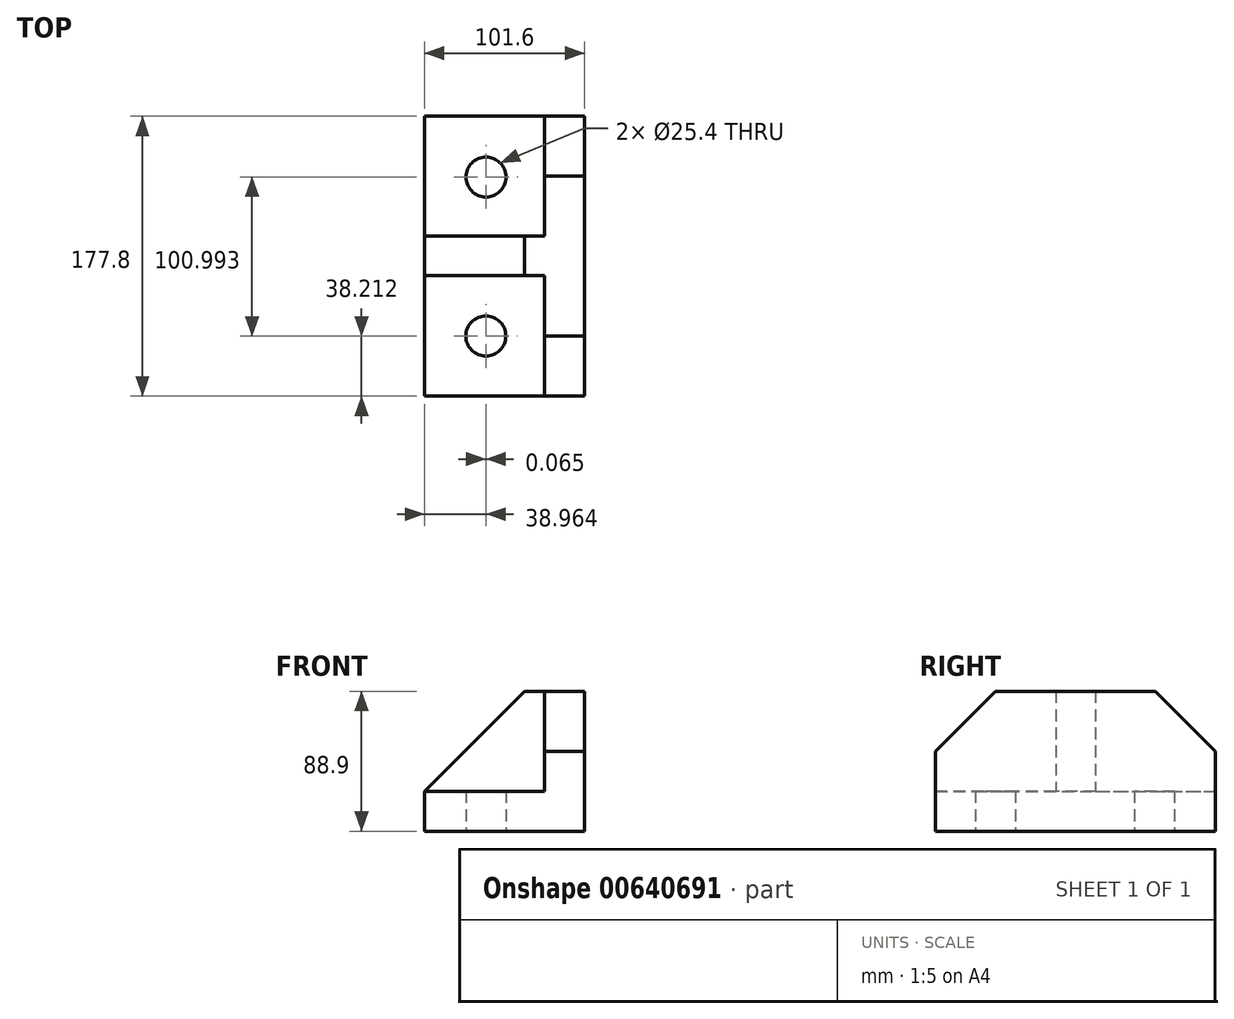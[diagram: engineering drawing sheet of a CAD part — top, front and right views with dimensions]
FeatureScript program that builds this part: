
annotation { "Feature Type Name" : "Feature", "Feature Type Description" : "" }
export const myFeature = defineFeature(function(context is Context, id is Id, definition is map)
    precondition{}
    {
        {
            var Q0;
            Q0=qCreatedBy(makeId("Top.planeOp"),FACE);
            var sketch = newSketch(context, id + "F0", { "sketchPlane" : qUnion([Q0])});
            skLineSegment(sketch, "E0", {"start": v(-50.08, -90.37) * mm, "end": v(51.52, -90.37) * mm});
            skLineSegment(sketch, "E1", {"start": v(-50.08, -90.37) * mm, "end": v(-50.08, 87.43) * mm});
            skLineSegment(sketch, "E2", {"start": v(-50.08, 87.43) * mm, "end": v(51.52, 87.43) * mm});
            skLineSegment(sketch, "E3", {"start": v(51.52, 87.43) * mm, "end": v(51.52, -90.37) * mm});
            skLineSegment(sketch, "E4", {"start": v(-50.08, 11.23) * mm, "end": v(51.52, 11.23) * mm});
            skLineSegment(sketch, "E5", {"start": v(51.52, -14.17) * mm, "end": v(-50.08, -14.17) * mm});
            skLineSegment(sketch, "E6", {"start": v(26.12, 87.43) * mm, "end": v(26.12, -90.37) * mm});
            skLineSegment(sketch, "E7", {"start": v(26.12, 49.33) * mm, "end": v(26.12, -52.27) * mm});
            skLineSegment(sketch, "E8", {"start": v(26.12, 49.33) * mm, "end": v(51.52, 49.33) * mm});
            skLineSegment(sketch, "E9", {"start": v(26.12, -52.27) * mm, "end": v(51.52, -52.27) * mm});
            skCircle(sketch, "E10", {"center": v(-11.05, 48.83) * mm, "radius": 12.7 * mm});
            skCircle(sketch, "E11", {"center": v(-11.12, -52.16) * mm, "radius": 12.7 * mm});
            skSolve(sketch);
        }
        {
            var Q0;
            {var subQ0=sQuery(id+"F0.wireOp",EDGE,"E4");var subQ1=sQuery(id+"F0.wireOp",EDGE,"E3");var subQ2=makeQuery(id+"F0.imprint","INTERSECT",VERTEX,{"derivedFrom":[subQ1,subQ0]});Q0=makeQuery(id+"F0.imprint","IMPRINT",FACE,{"disambiguationData":[TD([[makeQuery(id+"F0.imprint","IMPRINT",EDGE,{"disambiguationData":[TD([[subQ2,-1.0]])],"derivedFrom":subQ1}),-1.0]])]});}
            var Q1;
            {var subQ3=sQuery(id+"F0.wireOp",EDGE,"E8");Q1=makeQuery(id+"F0.imprint","IMPRINT",FACE,{"disambiguationData":[TD([[makeQuery(id+"F0.imprint","IMPRINT",EDGE,{"derivedFrom":subQ3}),-1.0]])]});}
            var Q2;
            {var subQ3=sQuery(id+"F0.wireOp",EDGE,"E9");Q2=makeQuery(id+"F0.imprint","IMPRINT",FACE,{"disambiguationData":[TD([[makeQuery(id+"F0.imprint","IMPRINT",EDGE,{"derivedFrom":subQ3}),1.0]])]});}
            extrude(context, id + "F1", {"entities" : qUnion([Q0, Q1, Q2]), "depth" : 88.9 * mm, "offsetDistance" : 25.4 * mm});
        }
        {
            var Q0;
            {var subQ1=sQuery(id+"F0.wireOp",EDGE,"E2");var subQ5=sQuery(id+"F0.wireOp",EDGE,"E1");var subQ6=makeQuery(id+"F0.imprint","INTERSECT",VERTEX,{"derivedFrom":[subQ5,subQ1]});Q0=makeQuery(id+"F0.imprint","IMPRINT",FACE,{"disambiguationData":[TD([[makeQuery(id+"F0.imprint","IMPRINT",EDGE,{"disambiguationData":[TD([[subQ6,1.0]])],"derivedFrom":subQ5}),-1.0]])]});}
            var Q1;
            {var subQ0=sQuery(id+"F0.wireOp",EDGE,"E4");var subQ1=sQuery(id+"F0.wireOp",EDGE,"E1");var subQ2=makeQuery(id+"F0.imprint","INTERSECT",VERTEX,{"derivedFrom":[subQ1,subQ0]});Q1=makeQuery(id+"F0.imprint","IMPRINT",FACE,{"disambiguationData":[TD([[makeQuery(id+"F0.imprint","IMPRINT",EDGE,{"disambiguationData":[TD([[subQ2,1.0]])],"derivedFrom":subQ1}),-1.0]])]});}
            var Q2;
            {var subQ1=sQuery(id+"F0.wireOp",EDGE,"E0");var subQ5=sQuery(id+"F0.wireOp",EDGE,"E1");var subQ6=makeQuery(id+"F0.imprint","INTERSECT",VERTEX,{"derivedFrom":[subQ1,subQ5]});Q2=makeQuery(id+"F0.imprint","IMPRINT",FACE,{"disambiguationData":[TD([[makeQuery(id+"F0.imprint","IMPRINT",EDGE,{"disambiguationData":[TD([[subQ6,-1.0]])],"derivedFrom":subQ1}),1.0]])]});}
            extrude(context, id + "F2", {"entities" : qUnion([Q0, Q1, Q2]), "operationType" : NewBodyOperationType.ADD, "depth" : 25.4 * mm, "offsetDistance" : 25.4 * mm});
        }
        {
            var Q0;
            Q0=makeQuery(id+"F0.imprint","IMPRINT",FACE,{"disambiguationData":[TD([[makeQuery(id+"F0.imprint","IMPRINT",EDGE,{"derivedFrom":sQuery(id+"F0.wireOp",EDGE,"E10")}),1.0]])]});
            var Q1;
            Q1=makeQuery(id+"F0.imprint","IMPRINT",FACE,{"disambiguationData":[TD([[makeQuery(id+"F0.imprint","IMPRINT",EDGE,{"derivedFrom":sQuery(id+"F0.wireOp",EDGE,"E11")}),1.0]])]});
            var Q2;
            Q2=sQuery(id+"F0.wireOp",EDGE,"E10");
            var Q3;
            Q3=sQuery(id+"F0.wireOp",EDGE,"E11");
            extrude(context, id + "F3", {"entities" : qUnion([Q0, Q1]), "operationType" : NewBodyOperationType.REMOVE, "surfaceEntities" : qUnion([Q2, Q3]), "oppositeDirection" : true, "depth" : 25.4 * mm, "offsetDistance" : 25.4 * mm});
        }
        {
            var Q0;
            Q0=makeQuery(id+"F2.opExtrude","CAP_FACE",FACE,{"disambiguationData":[OSD([sQuery(id+"F0.wireOp",EDGE,"E0"),sQuery(id+"F0.wireOp",EDGE,"E1"),sQuery(id+"F0.wireOp",EDGE,"E2"),sQuery(id+"F0.wireOp",EDGE,"E6"),sQuery(id+"F0.wireOp",EDGE,"E7"),sQuery(id+"F0.wireOp",EDGE,"E10"),sQuery(id+"F0.wireOp",EDGE,"E11")])],"isStart":false});
            var sketch = newSketch(context, id + "F4", { "sketchPlane" : qUnion([Q0])});
            skPoint(sketch, "E12", {"position": v(-50.08, 11.34) * mm});
            skPoint(sketch, "E13", {"position": v(-50.08, -14.28) * mm});
            skSolve(sketch);
        }
        {
            var Q0;
            {var subQ3=sQuery(id+"F0.wireOp",EDGE,"E0");Q0=makeQuery(id+"F4.imprint","IMPRINT",FACE,{"disambiguationData":[TD([[makeQuery(id+"F4.imprint","IMPRINT",EDGE,{"derivedFrom":makeQuery(id+"F2.opExtrude","CAP_EDGE",EDGE,{"disambiguationData":[OSD([subQ3])],"isStart":false})}),1.0]])]});}
            var sketch = newSketch(context, id + "F5", { "sketchPlane" : qUnion([Q0])});
            skLineSegment(sketch, "E14.bottom", {"start": v(-49.99, 11.32) * mm, "end": v(26.12, 11.32) * mm});
            skLineSegment(sketch, "E14.top", {"start": v(-49.99, -13.92) * mm, "end": v(26.12, -13.92) * mm});
            skLineSegment(sketch, "E14.left", {"start": v(-49.99, 11.32) * mm, "end": v(-49.99, -13.92) * mm});
            skLineSegment(sketch, "E14.right", {"start": v(26.12, 11.32) * mm, "end": v(26.12, -13.92) * mm});
            skSolve(sketch);
        }
        {
            var Q0;
            Q0=makeQuery(id+"F5.imprint","IMPRINT",FACE,{"disambiguationData":[TD([[makeQuery(id+"F5.imprint","IMPRINT",EDGE,{"derivedFrom":sQuery(id+"F5.wireOp",EDGE,"E14.bottom")}),-1.0]])]});
            extrude(context, id + "F6", {"entities" : qUnion([Q0]), "operationType" : NewBodyOperationType.ADD, "depth" : 63.5 * mm, "offsetDistance" : 25.4 * mm});
        }
        {
            var Q0;
            Q0=makeQuery(id+"F6.opExtrude","CAP_EDGE",EDGE,{"disambiguationData":[OSD([sQuery(id+"F5.wireOp",EDGE,"E14.left")])],"isStart":false});
            chamfer(context, id + "F7", {"entities" : qUnion([Q0]), "width" : 63.5 * mm, "tangentPropagation" : true});
        }
        {
            var Q0;
            Q0=makeQuery(id+"F1.opExtrude","SWEPT_FACE",FACE,{"disambiguationData":[OSD([sQuery(id+"F0.wireOp",EDGE,"E9")])]});
            extrude(context, id + "F8", {"entities" : qUnion([Q0]), "operationType" : NewBodyOperationType.ADD, "depth" : 38.1 * mm, "offsetDistance" : 25.4 * mm});
        }
        {
            var Q0;
            {var subQ0=sQuery(id+"F0.wireOp",EDGE,"E9");Q0=makeQuery(id+"F8.opExtrude","CAP_EDGE",EDGE,{"disambiguationData":[OSD([subQ0]),TDD([makeQuery(id+"F1.opExtrude","CAP_EDGE",EDGE,{"disambiguationData":[OSD([subQ0])],"isStart":false})])],"isStart":false});}
            chamfer(context, id + "F9", {"entities" : qUnion([Q0]), "width" : 38.1 * mm, "tangentPropagation" : true});
        }
        {
            var Q0;
            Q0=makeQuery(id+"F1.opExtrude","SWEPT_FACE",FACE,{"disambiguationData":[OSD([sQuery(id+"F0.wireOp",EDGE,"E8")])]});
            extrude(context, id + "F10", {"entities" : qUnion([Q0]), "operationType" : NewBodyOperationType.ADD, "depth" : 38.1 * mm, "offsetDistance" : 25.4 * mm});
        }
        {
            var Q0;
            {var subQ0=sQuery(id+"F0.wireOp",EDGE,"E8");Q0=makeQuery(id+"F10.opExtrude","CAP_EDGE",EDGE,{"disambiguationData":[OSD([subQ0]),TDD([makeQuery(id+"F1.opExtrude","CAP_EDGE",EDGE,{"disambiguationData":[OSD([subQ0])],"isStart":false})])],"isStart":false});}
            chamfer(context, id + "F11", {"entities" : qUnion([Q0]), "width" : 38.1 * mm, "tangentPropagation" : true});
        }
    });
